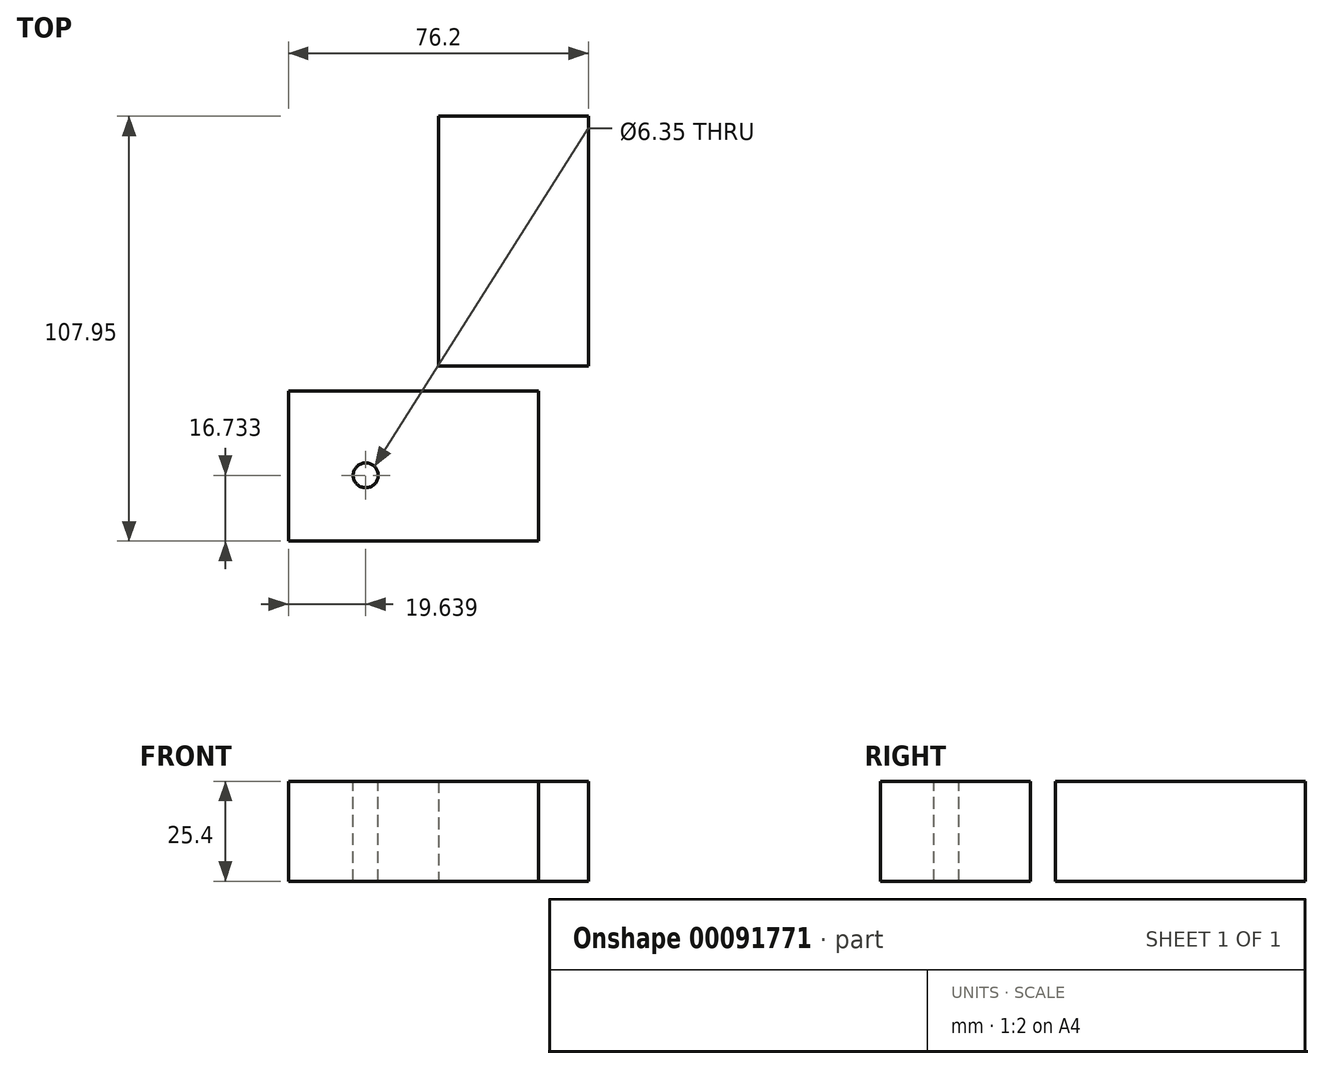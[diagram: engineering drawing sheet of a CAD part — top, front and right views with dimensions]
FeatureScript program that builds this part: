
annotation { "Feature Type Name" : "Feature", "Feature Type Description" : "" }
export const myFeature = defineFeature(function(context is Context, id is Id, definition is map)
    precondition{}
    {
        {
            var Q0;
            Q0=qCreatedBy(makeId("Top.planeOp"),FACE);
            var sketch = newSketch(context, id + "F0", { "sketchPlane" : qUnion([Q0])});
            skLineSegment(sketch, "E0.bottom", {"start": v(0, 0) * mm, "end": v(63.5, 0) * mm});
            skLineSegment(sketch, "E0.top", {"start": v(0, -38.1) * mm, "end": v(63.5, -38.1) * mm});
            skLineSegment(sketch, "E0.left", {"start": v(0, 0) * mm, "end": v(0, -38.1) * mm});
            skLineSegment(sketch, "E0.right", {"start": v(63.5, 0) * mm, "end": v(63.5, -38.1) * mm});
            skLineSegment(sketch, "E1.bottom", {"start": v(38.1, 6.35) * mm, "end": v(76.2, 6.35) * mm});
            skLineSegment(sketch, "E1.top", {"start": v(38.1, 69.85) * mm, "end": v(76.2, 69.85) * mm});
            skLineSegment(sketch, "E1.left", {"start": v(38.1, 6.35) * mm, "end": v(38.1, 69.85) * mm});
            skLineSegment(sketch, "E1.right", {"start": v(76.2, 6.35) * mm, "end": v(76.2, 69.85) * mm});
            skSolve(sketch);
        }
        {
            var Q0;
            Q0=makeQuery(id+"F0.imprint","IMPRINT",FACE,{"disambiguationData":[TD([[makeQuery(id+"F0.imprint","IMPRINT",EDGE,{"derivedFrom":sQuery(id+"F0.wireOp",EDGE,"E0.bottom")}),-1.0]])]});
            var Q1;
            Q1=makeQuery(id+"F0.imprint","IMPRINT",FACE,{"disambiguationData":[TD([[makeQuery(id+"F0.imprint","IMPRINT",EDGE,{"derivedFrom":sQuery(id+"F0.wireOp",EDGE,"E1.bottom")}),1.0]])]});
            extrude(context, id + "F1", {"entities" : qUnion([Q0, Q1]), "depth" : 25.4 * mm});
        }
        {
            var Q0;
            Q0=makeQuery(id+"F1.opExtrude","CAP_FACE",FACE,{"disambiguationData":[OSD([sQuery(id+"F0.wireOp",EDGE,"E0.bottom"),sQuery(id+"F0.wireOp",EDGE,"E0.top"),sQuery(id+"F0.wireOp",EDGE,"E0.left"),sQuery(id+"F0.wireOp",EDGE,"E0.right")])],"isStart":false});
            var sketch = newSketch(context, id + "F2", { "sketchPlane" : qUnion([Q0])});
            skPoint(sketch, "E2", {"position": v(19.64, -21.37) * mm});
            skSolve(sketch);
        }
        {
            var Q0;
            Q0=sQuery(id+"F2.wireOp",VERTEX,"E2");
            var Q1;
            Q1=makeQuery(id+"F1.opExtrude","SWEPT_BODY",BODY,{"disambiguationData":[OSD([sQuery(id+"F0.wireOp",EDGE,"E0.bottom"),sQuery(id+"F0.wireOp",EDGE,"E0.top"),sQuery(id+"F0.wireOp",EDGE,"E0.left"),sQuery(id+"F0.wireOp",EDGE,"E0.right")])]});
            hole(context, id + "F3", {"style" : HoleStyle.SIMPLE, "endStyle" : HoleEndStyle.THROUGH, "holeDiameter" : 6.35 * mm, "locations" : qUnion([Q0]), "scope" : qUnion([Q1]), "isTappedThrough" : true});
        }
    });
